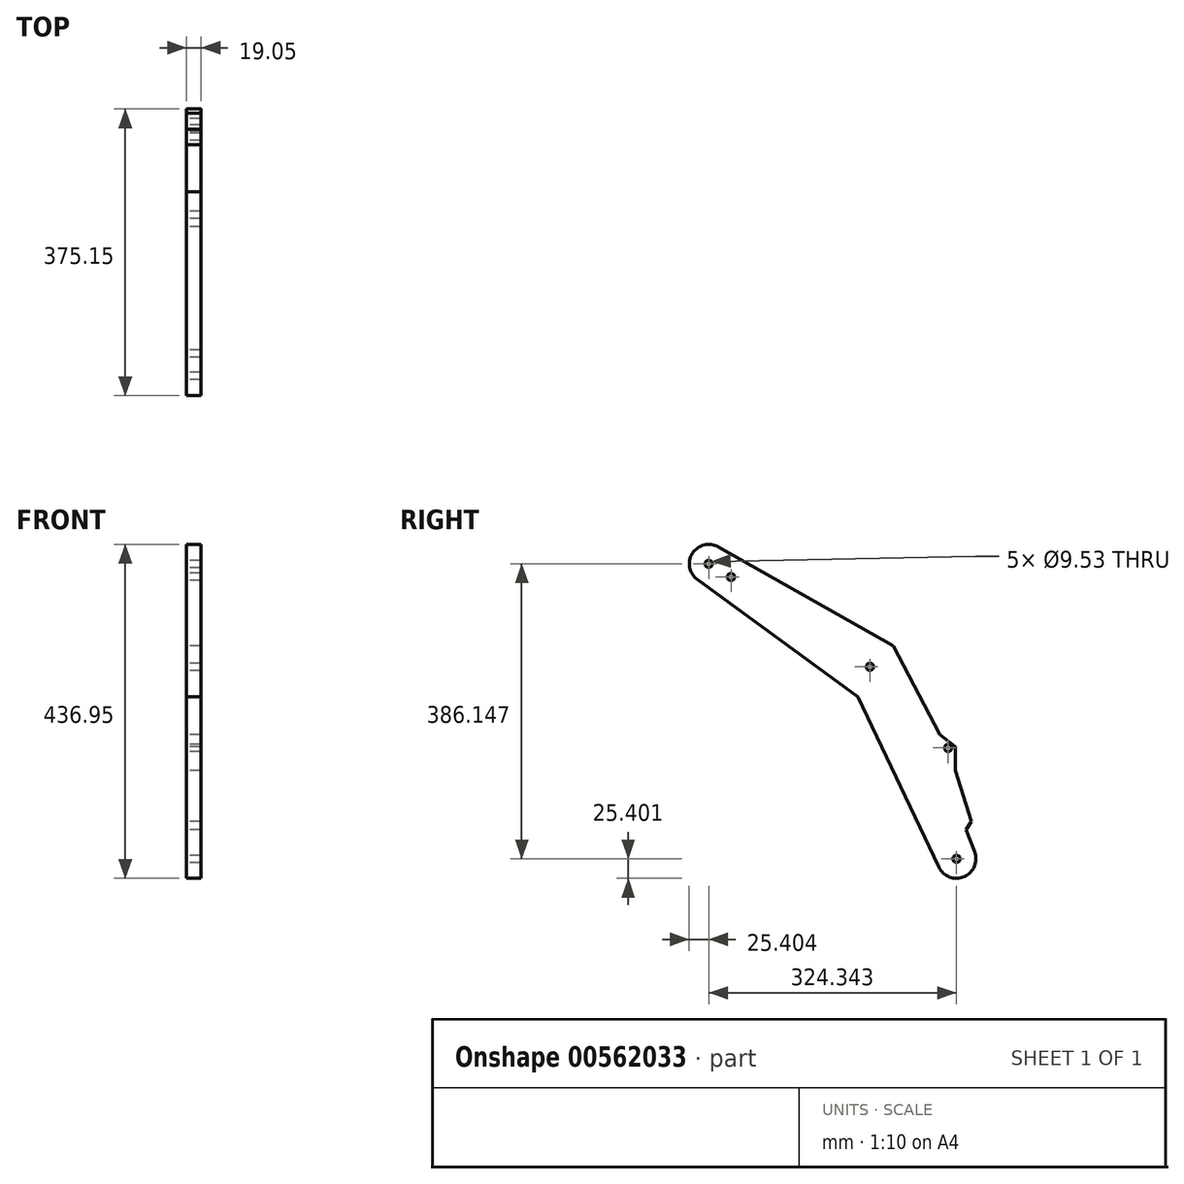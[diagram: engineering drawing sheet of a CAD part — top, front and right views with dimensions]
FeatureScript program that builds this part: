
annotation { "Feature Type Name" : "Feature", "Feature Type Description" : "" }
export const myFeature = defineFeature(function(context is Context, id is Id, definition is map)
    precondition{}
    {
        {
            var Q0;
            Q0=qCreatedBy(makeId("Right.planeOp"),FACE);
            var sketch = newSketch(context, id + "F0", { "sketchPlane" : qUnion([Q0])});
            skLineSegment(sketch, "E0", {"start": v(-513.86, 319.86) * mm, "end": v(-513.86, 78.56) * mm});
            skSolve(sketch);
        }
        {
            var Q0;
            Q0=qCreatedBy(makeId("Right.planeOp"),FACE);
            var sketch = newSketch(context, id + "F1", { "sketchPlane" : qUnion([Q0])});
            skLineSegment(sketch, "E1", {"start": v(-749.76, 256.37) * mm, "end": v(-601.81, 261.03) * mm});
            skLineSegment(sketch, "E2", {"start": v(-560.54, 653.66) * mm, "end": v(-601.81, 261.03) * mm});
            skLineSegment(sketch, "E3", {"start": v(-560.54, 653.66) * mm, "end": v(-749.76, 256.37) * mm});
            skLineSegment(sketch, "E4", {"start": v(-712.77, 291.22) * mm, "end": v(-723.7, 436.42) * mm});
            skLineSegment(sketch, "E5", {"start": v(-712.77, 291.22) * mm, "end": v(-826.16, 542.64) * mm});
            skLineSegment(sketch, "E6", {"start": v(-723.7, 436.42) * mm, "end": v(-826.16, 542.64) * mm});
            skLineSegment(sketch, "E7", {"start": v(-1007.93, 660.27) * mm, "end": v(-826.16, 542.64) * mm});
            skLineSegment(sketch, "E8", {"start": v(-1037.12, 677.37) * mm, "end": v(-1007.93, 660.27) * mm});
            skLineSegment(sketch, "E9", {"start": v(-1037.12, 677.37) * mm, "end": v(-712.77, 291.22) * mm});
            skLineSegment(sketch, "E10", {"start": v(-1007.93, 660.27) * mm, "end": v(-712.77, 291.22) * mm});
            skLineSegment(sketch, "E11", {"start": v(-601.81, 261.03) * mm, "end": v(-595.01, 401.75) * mm});
            skLineSegment(sketch, "E12", {"start": v(-601.81, 261.03) * mm, "end": v(-607.25, 655.88) * mm});
            skLineSegment(sketch, "E13", {"start": v(-595.01, 401.75) * mm, "end": v(-607.25, 655.88) * mm});
            skLineSegment(sketch, "E14", {"start": v(-723.7, 436.42) * mm, "end": v(-595.01, 401.75) * mm});
            skLineSegment(sketch, "E15", {"start": v(-826.16, 542.64) * mm, "end": v(-774.61, 590.25) * mm});
            skLineSegment(sketch, "E16", {"start": v(-749.76, 256.37) * mm, "end": v(-774.61, 590.25) * mm});
            skLineSegment(sketch, "E17", {"start": v(-1041.29, 793.41) * mm, "end": v(-774.61, 590.25) * mm});
            skLineSegment(sketch, "E18", {"start": v(-1390.78, 317.95) * mm, "end": v(-1336.8, 360.93) * mm});
            skLineSegment(sketch, "E19", {"start": v(-1336.8, 360.93) * mm, "end": v(-1295.1, 301.57) * mm});
            skLineSegment(sketch, "E20", {"start": v(-1041.29, 793.41) * mm, "end": v(-1295.1, 301.57) * mm});
            skLineSegment(sketch, "E21", {"start": v(-1295.1, 301.57) * mm, "end": v(-1037.12, 677.37) * mm});
            skLineSegment(sketch, "E22", {"start": v(-1037.12, 677.37) * mm, "end": v(-1041.29, 793.41) * mm});
            skLineSegment(sketch, "E23", {"start": v(-1007.93, 660.27) * mm, "end": v(-1336.8, 360.93) * mm});
            skLineSegment(sketch, "E24", {"start": v(-1390.78, 317.95) * mm, "end": v(-1295.1, 301.57) * mm});
            skLineSegment(sketch, "E25", {"start": v(-1295.1, 301.57) * mm, "end": v(-1295.1, 192.57) * mm});
            skLineSegment(sketch, "E26", {"start": v(-1295.1, 192.57) * mm, "end": v(-1403.22, 211.07) * mm});
            skLineSegment(sketch, "E27", {"start": v(-1403.22, 211.07) * mm, "end": v(-1390.78, 317.95) * mm});
            skLineSegment(sketch, "E28", {"start": v(-1390.78, 317.95) * mm, "end": v(-1295.1, 192.57) * mm});
            skLineSegment(sketch, "E29", {"start": v(0, 0) * mm, "end": v(0, 674.17) * mm});
            skLineSegment(sketch, "E30", {"start": v(-316.61, 320.6) * mm, "end": v(-316.61, 307.94) * mm});
            skLineSegment(sketch, "E31", {"start": v(-400.45, 218.07) * mm, "end": v(-378.01, 218.07) * mm});
            skLineSegment(sketch, "E32", {"start": v(-472.6, 74.76) * mm, "end": v(-472.6, 54.94) * mm});
            skSolve(sketch);
        }
        {
            var Q0;
            Q0=qCreatedBy(makeId("Right.planeOp"),FACE);
            var sketch = newSketch(context, id + "F2", { "sketchPlane" : qUnion([Q0])});
            skLineSegment(sketch, "E33", {"start": v(-1052.1, 656.86) * mm, "end": v(-841.88, 503.26) * mm});
            skLineSegment(sketch, "E34", {"start": v(-841.88, 503.26) * mm, "end": v(-735.7, 280.3) * mm});
            skLineSegment(sketch, "E35", {"start": v(-689.06, 300.33) * mm, "end": v(-700.26, 329.46) * mm});
            skLineSegment(sketch, "E36", {"start": v(-700.26, 329.46) * mm, "end": v(-693.15, 340.5) * mm});
            skLineSegment(sketch, "E37", {"start": v(-693.15, 340.5) * mm, "end": v(-714.2, 407.11) * mm});
            skLineSegment(sketch, "E38", {"start": v(-714.2, 407.11) * mm, "end": v(-714.2, 438.2) * mm});
            skLineSegment(sketch, "E39", {"start": v(-714.2, 438.2) * mm, "end": v(-734.42, 453.7) * mm});
            skLineSegment(sketch, "E40", {"start": v(-734.42, 453.7) * mm, "end": v(-795.7, 569.95) * mm});
            skLineSegment(sketch, "E41", {"start": v(-795.7, 569.95) * mm, "end": v(-1024.6, 699.47) * mm});
            skArc(sketch, "E42", {"start": v(-1052.1, 656.86) * mm, "mid": v(-1058.46, 691.14) * mm, "end": v(-1024.6, 699.47) * mm});
            skArc(sketch, "E43", {"start": v(-735.7, 280.3) * mm, "mid": v(-702.75, 267.88) * mm, "end": v(-689.06, 300.33) * mm});
            skCircle(sketch, "E44", {"center": v(-1037.12, 677.37) * mm, "radius": 4.76 * mm});
            skCircle(sketch, "E45", {"center": v(-826.16, 542.64) * mm, "radius": 4.76 * mm});
            skCircle(sketch, "E46", {"center": v(-723.7, 436.42) * mm, "radius": 4.76 * mm});
            skCircle(sketch, "E47", {"center": v(-712.77, 291.22) * mm, "radius": 4.76 * mm});
            skCircle(sketch, "E48", {"center": v(-1007.93, 660.27) * mm, "radius": 4.76 * mm});
            skSolve(sketch);
        }
        {
            var Q0;
            Q0=qSketchRegion(id+"F2",true);
            extrude(context, id + "F3", {"entities" : qUnion([Q0]), "depth" : 19.05 * mm, "offsetDistance" : 25.4 * mm});
        }
    });
